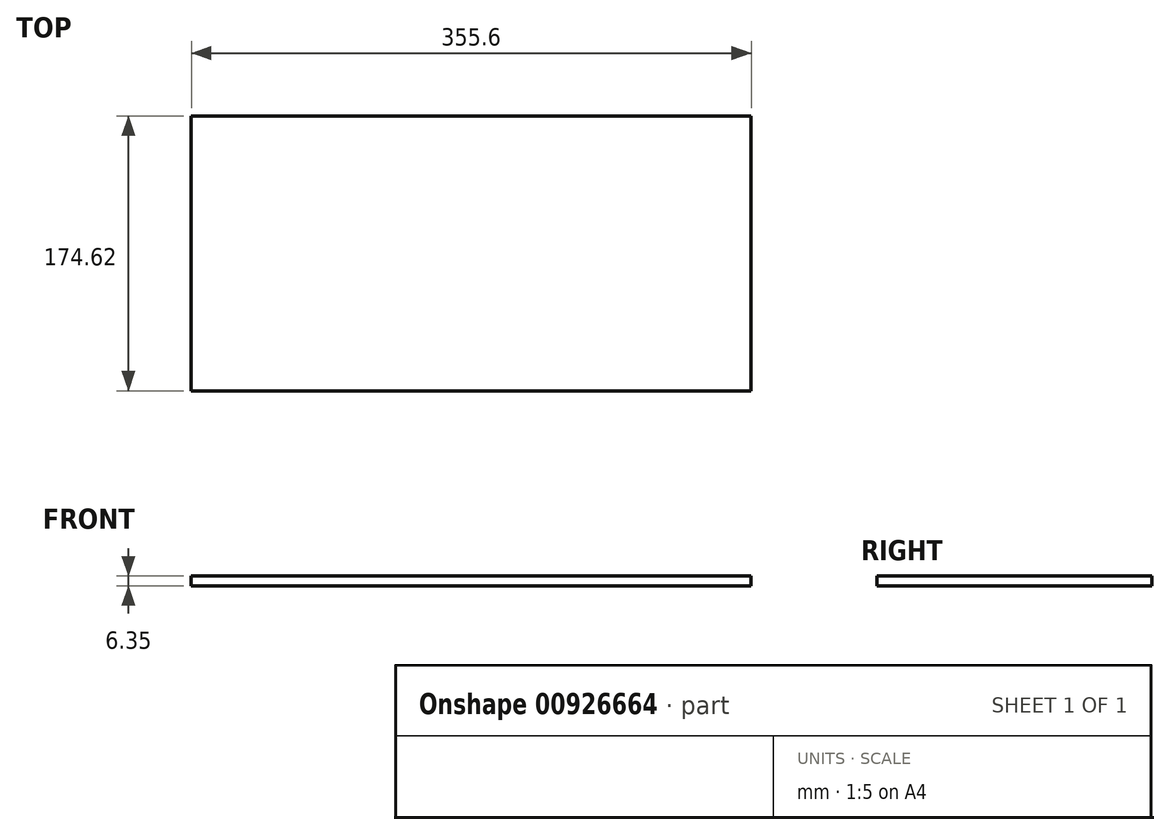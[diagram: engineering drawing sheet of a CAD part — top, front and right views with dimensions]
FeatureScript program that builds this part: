
annotation { "Feature Type Name" : "Feature", "Feature Type Description" : "" }
export const myFeature = defineFeature(function(context is Context, id is Id, definition is map)
    precondition{}
    {
        {
            var Q0;
            Q0=qCreatedBy(makeId("Top.planeOp"),FACE);
            var sketch = newSketch(context, id + "F0", { "sketchPlane" : qUnion([Q0])});
            skLineSegment(sketch, "E0.bottom", {"start": v(-152.12, 57.84) * mm, "end": v(203.48, 57.84) * mm});
            skLineSegment(sketch, "E0.top", {"start": v(-152.12, -116.78) * mm, "end": v(203.48, -116.78) * mm});
            skLineSegment(sketch, "E0.left", {"start": v(-152.12, 57.84) * mm, "end": v(-152.12, -116.78) * mm});
            skLineSegment(sketch, "E0.right", {"start": v(203.48, 57.84) * mm, "end": v(203.48, -116.78) * mm});
            skSolve(sketch);
        }
        {
            var Q0;
            Q0=makeQuery(id+"F0.imprint","IMPRINT",FACE,{"disambiguationData":[TD([[makeQuery(id+"F0.imprint","IMPRINT",EDGE,{"derivedFrom":sQuery(id+"F0.wireOp",EDGE,"E0.bottom")}),-1.0]])]});
            extrude(context, id + "F1", {"entities" : qUnion([Q0]), "depth" : 6.35 * mm, "offsetDistance" : 25.4 * mm});
        }
    });
